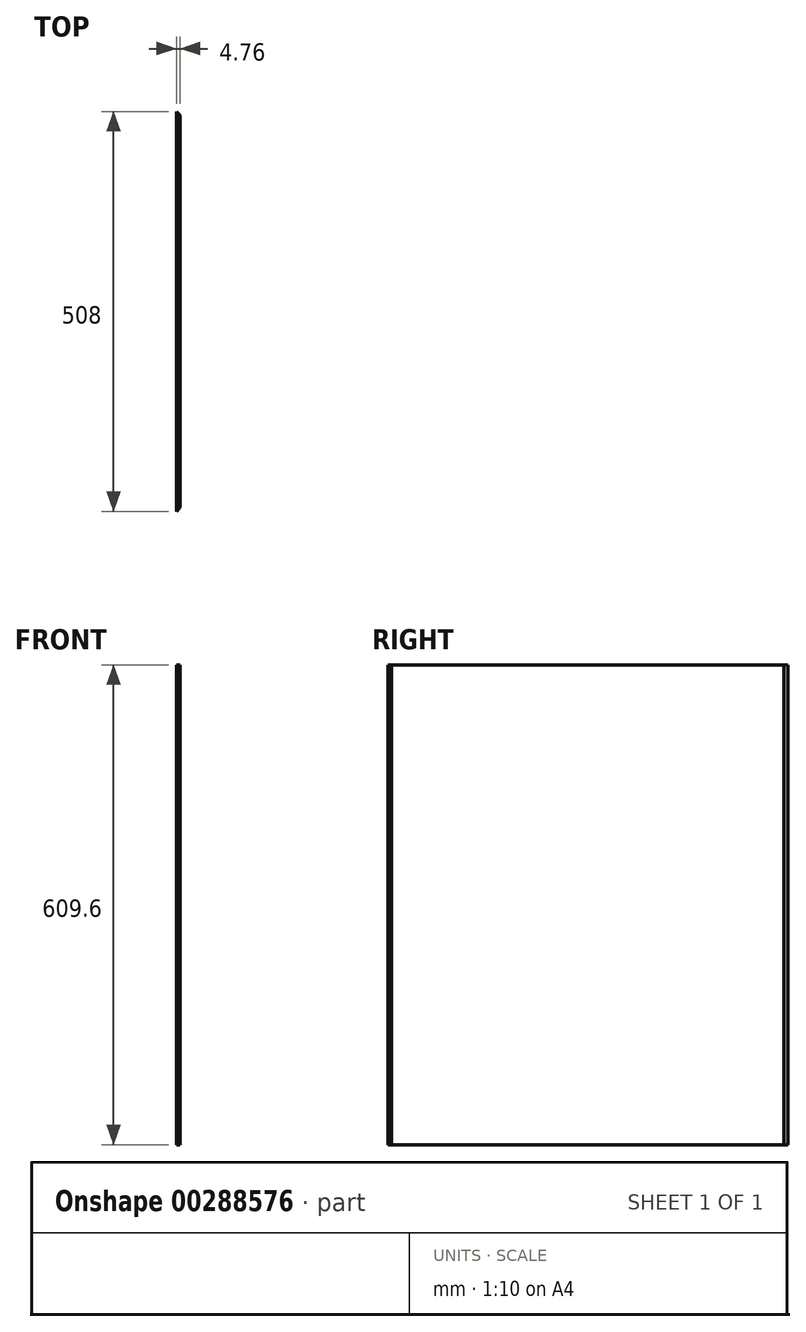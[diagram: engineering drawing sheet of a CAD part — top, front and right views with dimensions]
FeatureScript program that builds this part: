
annotation { "Feature Type Name" : "Feature", "Feature Type Description" : "" }
export const myFeature = defineFeature(function(context is Context, id is Id, definition is map)
    precondition{}
    {
        {
            var Q0;
            Q0=qCreatedBy(makeId("Right.planeOp"),FACE);
            var sketch = newSketch(context, id + "F0", { "sketchPlane" : qUnion([Q0])});
            skLineSegment(sketch, "E0.bottom", {"start": v(254, 304.8) * mm, "end": v(-254, 304.8) * mm});
            skLineSegment(sketch, "E0.top", {"start": v(254, -304.8) * mm, "end": v(-254, -304.8) * mm});
            skLineSegment(sketch, "E0.left", {"start": v(254, 304.8) * mm, "end": v(254, -304.8) * mm});
            skLineSegment(sketch, "E0.right", {"start": v(-254, 304.8) * mm, "end": v(-254, -304.8) * mm});
            skPoint(sketch, "E0.middle", {"position": v(0, 0) * mm});
            skSolve(sketch);
        }
        {
            var Q0;
            Q0 = qSketchRegion(id + "F0", true);
            extrude(context, id + "F1", {"entities" : qUnion([Q0]), "depth" : 4.76 * mm});
        }
        {
            var Q0;
            Q0=makeQuery(id+"F1.opExtrude","SWEPT_FACE",FACE,{"disambiguationData":[OSD([sQuery(id+"F0.wireOp",EDGE,"E0.bottom")])]});
            var sketch = newSketch(context, id + "F2", { "sketchPlane" : qUnion([Q0])});
            skLineSegment(sketch, "E1", {"start": v(4.76, -254) * mm, "end": v(0, -254) * mm});
            skLineSegment(sketch, "E2", {"start": v(0, -254) * mm, "end": v(4.76, -249.24) * mm});
            skLineSegment(sketch, "E3", {"start": v(4.76, -249.24) * mm, "end": v(4.76, -254) * mm});
            skSolve(sketch);
        }
        {
            var Q0;
            Q0=makeQuery(id+"F2.imprint","IMPRINT",FACE,{"disambiguationData":[TD([[makeQuery(id+"F2.imprint","IMPRINT",EDGE,{"derivedFrom":sQuery(id+"F2.wireOp",EDGE,"E1")}),-1.0]])]});
            extrude(context, id + "F3", {"entities" : qUnion([Q0]), "operationType" : NewBodyOperationType.REMOVE, "endBound" : BoundingType.THROUGH_ALL, "oppositeDirection" : true, "depth" : 25.4 * mm});
        }
        {
            var Q0;
            Q0=makeQuery(id+"F1.opExtrude","SWEPT_FACE",FACE,{"disambiguationData":[OSD([sQuery(id+"F0.wireOp",EDGE,"E0.bottom")])]});
            var sketch = newSketch(context, id + "F4", { "sketchPlane" : qUnion([Q0])});
            skLineSegment(sketch, "E4", {"start": v(4.76, 254) * mm, "end": v(0, 254) * mm});
            skLineSegment(sketch, "E5", {"start": v(0, 254) * mm, "end": v(4.76, 249.24) * mm});
            skLineSegment(sketch, "E6", {"start": v(4.76, 254) * mm, "end": v(4.76, 249.24) * mm});
            skSolve(sketch);
        }
        {
            var Q0;
            Q0=makeQuery(id+"F4.imprint","IMPRINT",FACE,{"disambiguationData":[TD([[makeQuery(id+"F4.imprint","IMPRINT",EDGE,{"derivedFrom":sQuery(id+"F4.wireOp",EDGE,"E4")}),1.0]])]});
            extrude(context, id + "F5", {"entities" : qUnion([Q0]), "operationType" : NewBodyOperationType.REMOVE, "endBound" : BoundingType.THROUGH_ALL, "oppositeDirection" : true, "depth" : 25.4 * mm});
        }
    });
